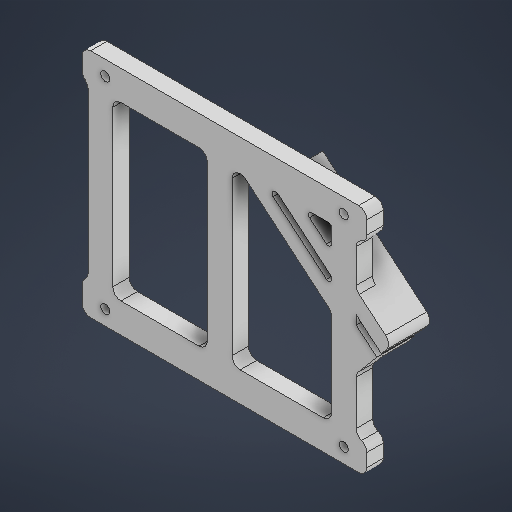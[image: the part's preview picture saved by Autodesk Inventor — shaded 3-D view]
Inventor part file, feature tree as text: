
AUTODESK INVENTOR PART (.ipt)
format: ipt  version: 2025 (Build 290162000, 162)  size: 366,080 bytes
history: native  units: mm
features: fillet x4, extrude x2, sketch x1
ambient origin geometry x8: Origin, YZ Plane, XZ Plane, XY Plane, X Axis, Y Axis, Z Axis, Center Point
bodies: Solid1 (feature_tree)
feature tree (7):
  sketch  "Sketch1"  dims[d7=24.5mm d8=49.0mm d9=58.0mm d10=58.0mm d11=2.2mm d12=2.2mm d13=2.2mm d14=2.2mm d15=69.2mm d16=7.2mm d17=69.2mm d18=7.2mm d19=6.0mm d20=6.0mm d21=4.0mm d22=0.0mm d23=6.0mm d24=0.0mm d36=6.0mm d37=35.0mm d38=24.43461mm d39=4.0mm d40=1.7mm d41=4.0mm d42=35.0mm d43=2.0mm d44=2.0mm d45=10.0mm d46=2.0mm d47=0.75mm]
  extrude  "Extrusion1"  Depth=49.0mm
  extrude  "Extrusion2"  Depth=0.75mm
  fillet  "Fillet5"  Radius=58.0mm
  fillet  "Fillet6"  Radius=2.2mm
  fillet  "Fillet7"  Radius=2.2mm
  fillet  "Fillet8"  Radius=2.2mm
